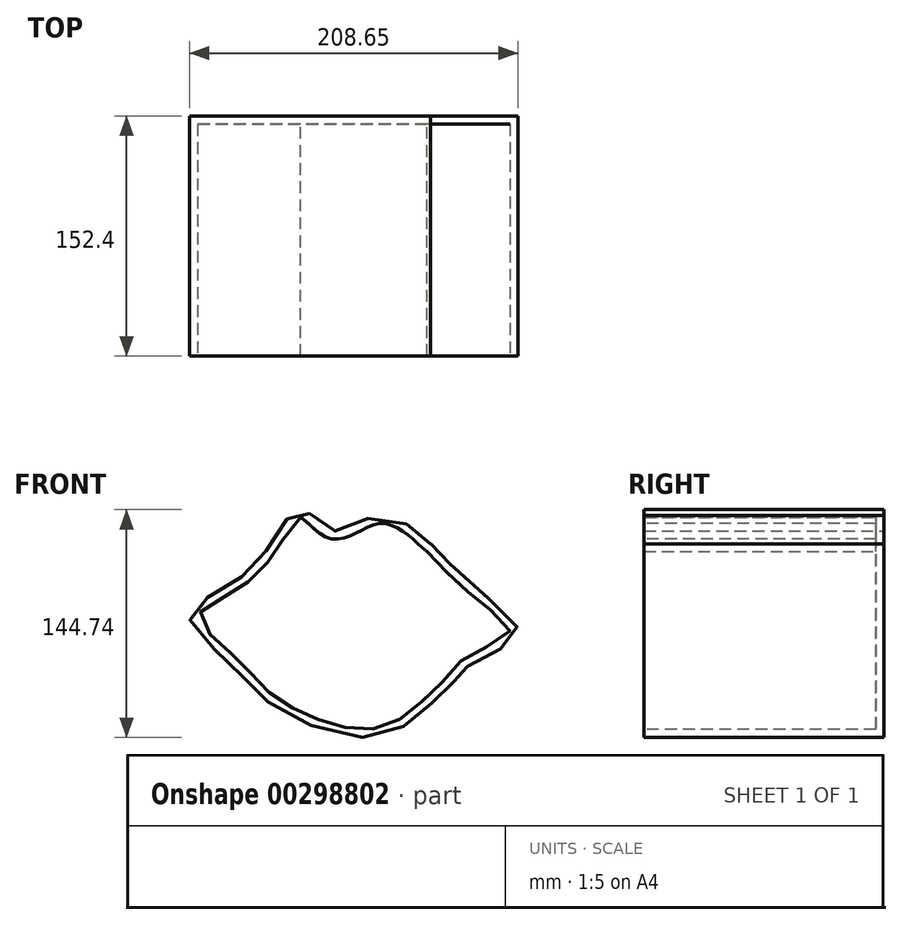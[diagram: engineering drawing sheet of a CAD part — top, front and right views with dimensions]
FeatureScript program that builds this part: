
annotation { "Feature Type Name" : "Feature", "Feature Type Description" : "" }
export const myFeature = defineFeature(function(context is Context, id is Id, definition is map)
    precondition{}
    {
        {
            var Q0;
            Q0=qCreatedBy(makeId("Front.planeOp"),FACE);
            var sketch = newSketch(context, id + "F0", { "sketchPlane" : qUnion([Q0])});
            skLineSegment(sketch, "E0.bottom", {"start": v(66, 66.57) * mm, "end": v(66.3, 66.57) * mm});
            skPoint(sketch, "E1.visualSharp", {"position": v(-60.7, 66.57) * mm});
            skPoint(sketch, "E2.visualSharp", {"position": v(-60.7, -35.03) * mm});
            skPoint(sketch, "E3.visualSharp", {"position": v(91.7, 66.57) * mm});
            skPoint(sketch, "E4.visualSharp", {"position": v(91.7, -35.03) * mm});
            skFitSpline(sketch, "E5", {"points": [v(66, 66.57) * mm, v(38.17, 84.54) * mm, v(4.2, 74.88) * mm, v(-16.03, 88.42) * mm, v(-35.3, 66.57) * mm, v(-60.7, 41.17) * mm, v(-86.96, 20.65) * mm, v(-60.7, -9.63) * mm, v(-35.3, -35.03) * mm, v(30.83, -55.98) * mm, v(66.3, -35.03) * mm, v(82.77, -18.93) * mm, v(91.7, -9.63) * mm, v(121.4, 9.25) * mm, v(91.7, 41.17) * mm, v(66.3, 66.57) * mm, v(66, 66.57) * mm]});
            skSolve(sketch);
        }
        {
            var Q0;
            Q0 = qSketchRegion(id + "F0", true);
            extrude(context, id + "F1", {"entities" : qUnion([Q0]), "depth" : 152.4 * mm});
        }
        {
            var Q0;
            Q0=makeQuery(id+"F1.opExtrude","CAP_FACE",FACE,{"disambiguationData":[OSD([sQuery(id+"F0.wireOp",EDGE,"E0.bottom"),sQuery(id+"F0.wireOp",EDGE,"E5")])],"isStart":false});
            shell(context, id + "F2", {"entities" : qUnion([Q0]), "thickness" : 5.08 * mm});
        }
    });
